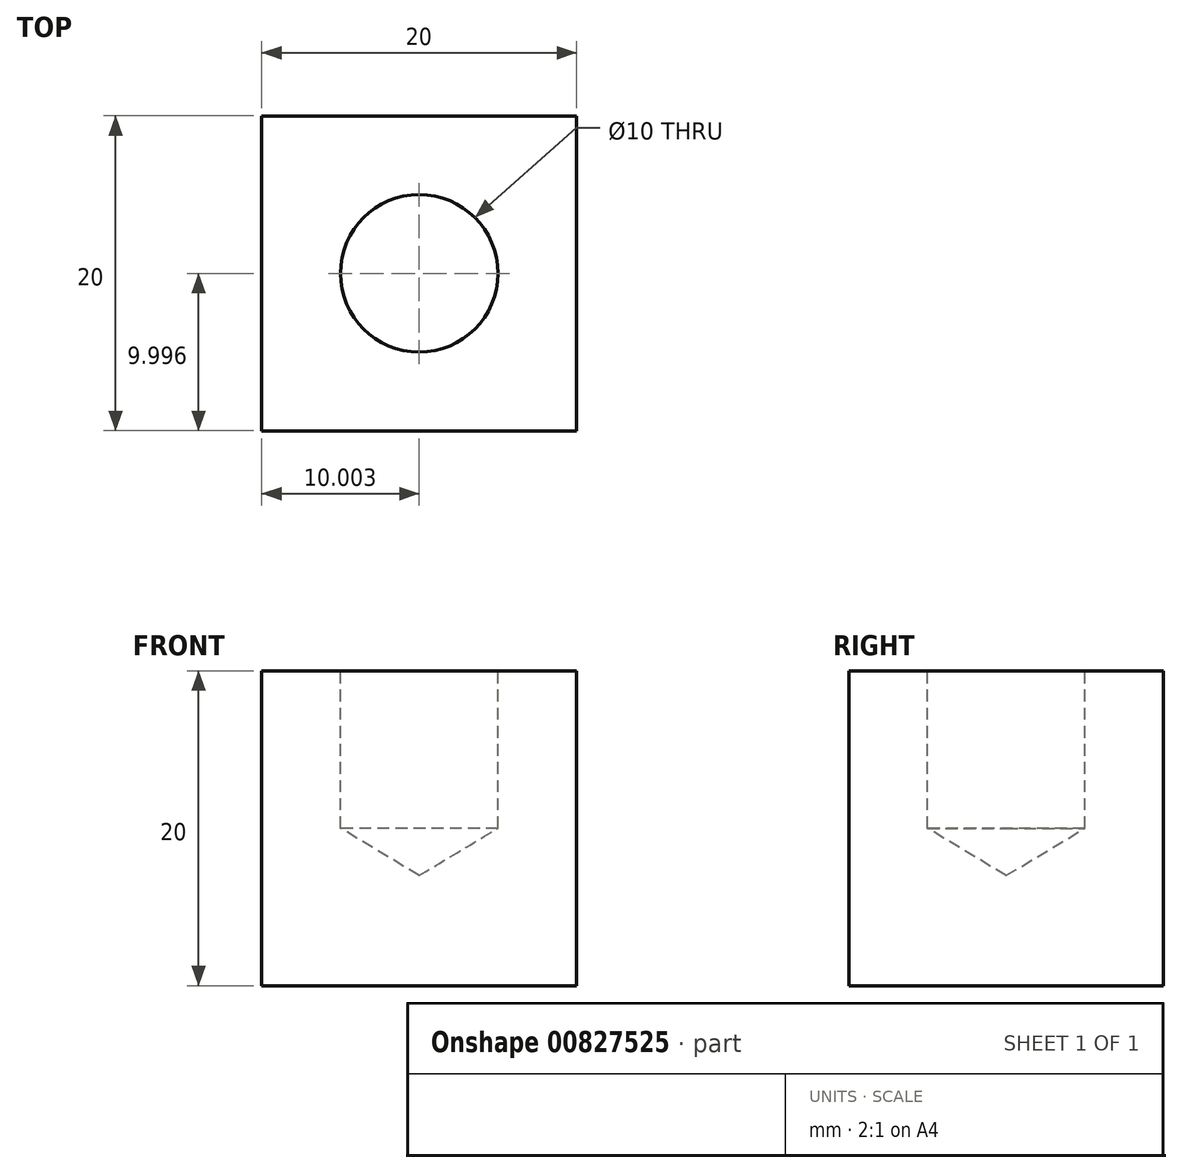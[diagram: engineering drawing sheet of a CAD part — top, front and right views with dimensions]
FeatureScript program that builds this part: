
annotation { "Feature Type Name" : "Feature", "Feature Type Description" : "" }
export const myFeature = defineFeature(function(context is Context, id is Id, definition is map)
    precondition{}
    {
        {
            var Q0;
            Q0=qCreatedBy(makeId("Top.planeOp"),FACE);
            var sketch = newSketch(context, id + "F0", { "sketchPlane" : qUnion([Q0])});
            skLineSegment(sketch, "E0", {"start": v(-13.32, -8.07) * mm, "end": v(-13.32, 11.93) * mm});
            skLineSegment(sketch, "E1", {"start": v(-13.32, 11.93) * mm, "end": v(6.68, 11.93) * mm});
            skLineSegment(sketch, "E2", {"start": v(6.68, 11.93) * mm, "end": v(6.68, -8.07) * mm});
            skLineSegment(sketch, "E3", {"start": v(6.68, -8.07) * mm, "end": v(-13.32, -8.07) * mm});
            skSolve(sketch);
        }
        {
            var Q0;
            Q0 = qSketchRegion(id + "F0", true);
            extrude(context, id + "F1", {"entities" : qUnion([Q0]), "depth" : 20 * mm, "offsetDistance" : 25 * mm});
        }
        {
            var Q0;
            Q0=makeQuery(id+"F1.opExtrude","CAP_FACE",FACE,{"disambiguationData":[OSD([sQuery(id+"F0.wireOp",EDGE,"E0"),sQuery(id+"F0.wireOp",EDGE,"E1"),sQuery(id+"F0.wireOp",EDGE,"E2"),sQuery(id+"F0.wireOp",EDGE,"E3")])],"isStart":false});
            var sketch = newSketch(context, id + "F2", { "sketchPlane" : qUnion([Q0])});
            skLineSegment(sketch, "E4", {"start": v(-13.32, 11.93) * mm, "end": v(6.68, -8.07) * mm});
            skLineSegment(sketch, "E5", {"start": v(-13.32, -8.07) * mm, "end": v(6.68, 11.93) * mm});
            skPoint(sketch, "E6", {"position": v(-3.32, 1.93) * mm});
            skSolve(sketch);
        }
        {
            var Q0;
            Q0=sQuery(id+"F2.wireOp",VERTEX,"E6");
            var Q1;
            Q1=makeQuery(id+"F1.opExtrude","SWEPT_BODY",BODY,{"disambiguationData":[OSD([sQuery(id+"F0.wireOp",EDGE,"E0"),sQuery(id+"F0.wireOp",EDGE,"E1"),sQuery(id+"F0.wireOp",EDGE,"E2"),sQuery(id+"F0.wireOp",EDGE,"E3")])]});
            hole(context, id + "F3", {"style" : HoleStyle.SIMPLE, "endStyle" : HoleEndStyle.BLIND, "holeDiameter" : 10 * mm, "majorDiameter" : 5 * mm, "holeDepth" : 10 * mm, "isTappedThrough" : true, "tappedDepth" : 12 * mm, "tapClearance" : 3, "startFromSketch" : true, "locations" : qUnion([Q0]), "scope" : qUnion([Q1])});
        }
    });
